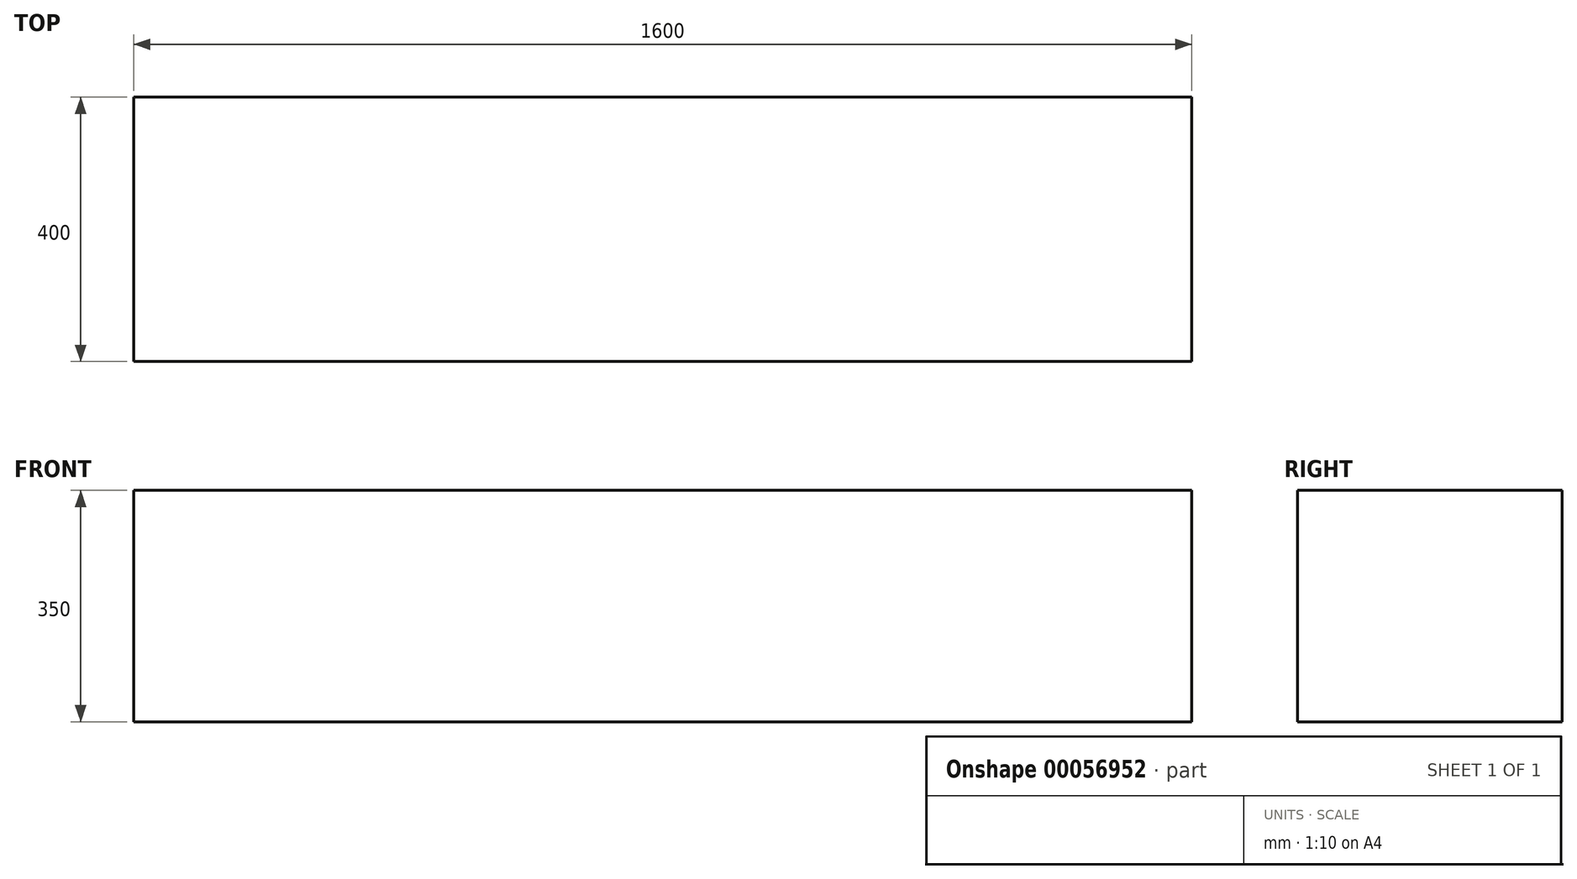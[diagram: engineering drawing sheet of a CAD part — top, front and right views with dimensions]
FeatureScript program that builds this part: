
annotation { "Feature Type Name" : "Feature", "Feature Type Description" : "" }
export const myFeature = defineFeature(function(context is Context, id is Id, definition is map)
    precondition{}
    {
        {
            var Q0;
            Q0=qCreatedBy(makeId("Top.planeOp"),FACE);
            var sketch = newSketch(context, id + "F0", { "sketchPlane" : qUnion([Q0])});
            skLineSegment(sketch, "E0.bottom", {"start": v(0, 0) * mm, "end": v(-1600, 0) * mm});
            skLineSegment(sketch, "E0.top", {"start": v(0, -400) * mm, "end": v(-1600, -400) * mm});
            skLineSegment(sketch, "E0.left", {"start": v(0, 0) * mm, "end": v(0, -400) * mm});
            skLineSegment(sketch, "E0.right", {"start": v(-1600, 0) * mm, "end": v(-1600, -400) * mm});
            skSolve(sketch);
        }
        {
            var Q0;
            Q0 = qSketchRegion(id + "F0", true);
            extrude(context, id + "F1", {"entities" : qUnion([Q0]), "depth" : 350 * mm});
        }
    });
